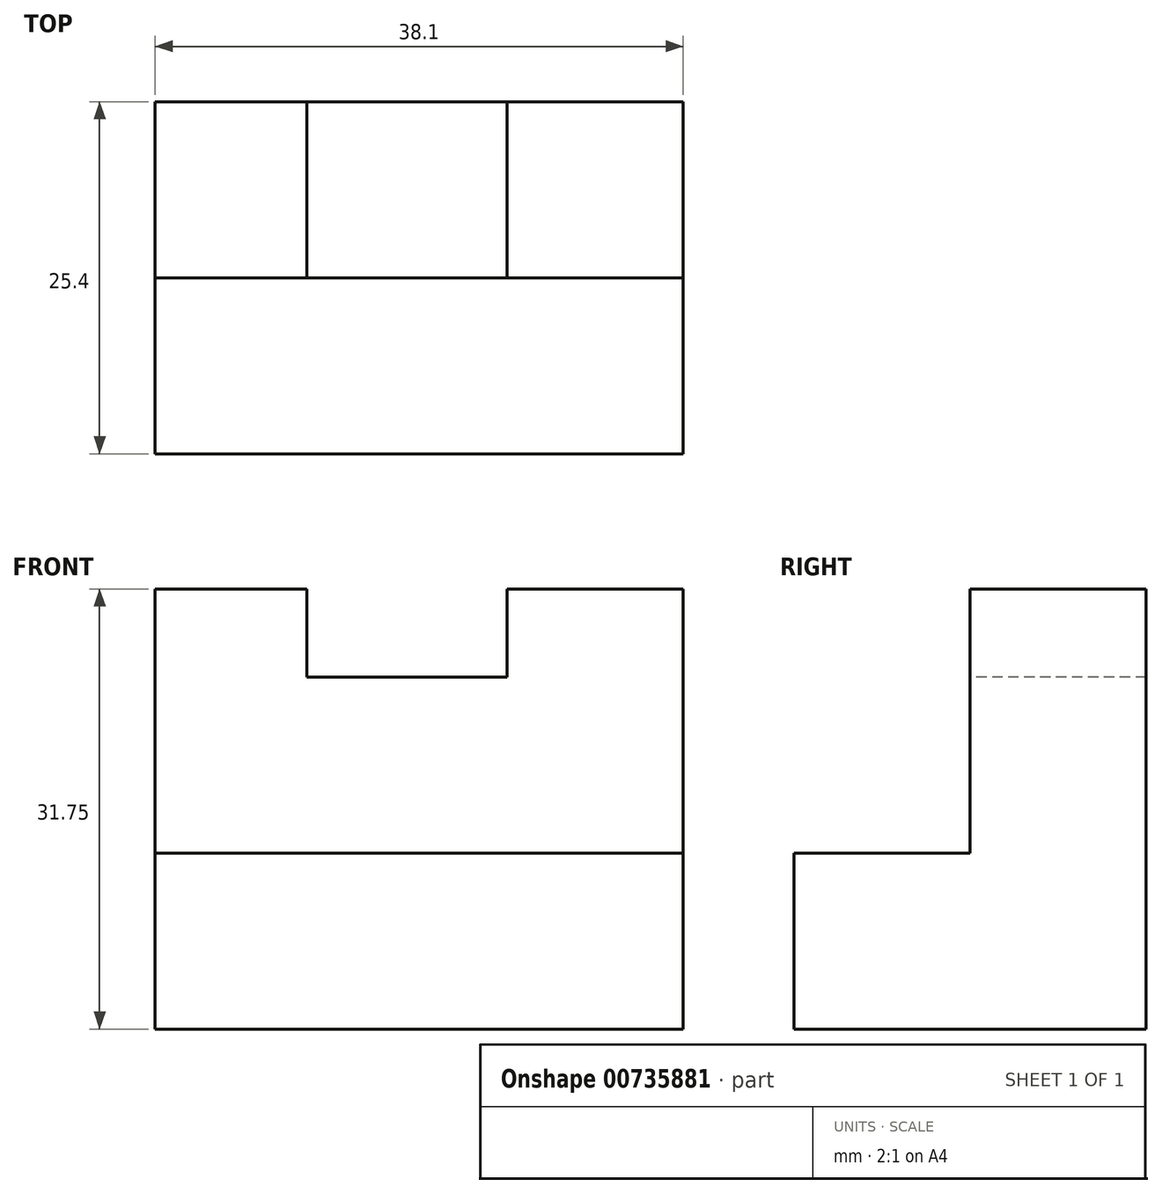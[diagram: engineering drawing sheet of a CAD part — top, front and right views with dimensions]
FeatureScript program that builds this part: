
annotation { "Feature Type Name" : "Feature", "Feature Type Description" : "" }
export const myFeature = defineFeature(function(context is Context, id is Id, definition is map)
    precondition{}
    {
        {
            var Q0;
            Q0=qCreatedBy(makeId("Right.planeOp"),FACE);
            var sketch = newSketch(context, id + "F0", { "sketchPlane" : qUnion([Q0])});
            skLineSegment(sketch, "E0", {"start": v(0, 0) * mm, "end": v(25.4, 0) * mm});
            skLineSegment(sketch, "E1", {"start": v(25.4, 0) * mm, "end": v(25.4, 31.75) * mm});
            skLineSegment(sketch, "E2", {"start": v(25.4, 31.75) * mm, "end": v(12.7, 31.75) * mm});
            skLineSegment(sketch, "E3", {"start": v(12.7, 31.75) * mm, "end": v(12.7, 12.7) * mm});
            skLineSegment(sketch, "E4", {"start": v(12.7, 12.7) * mm, "end": v(0, 12.7) * mm});
            skLineSegment(sketch, "E5", {"start": v(0, 12.7) * mm, "end": v(0, 0) * mm});
            skSolve(sketch);
        }
        {
            var Q0;
            Q0=makeQuery(id+"F0.imprint","IMPRINT",FACE,{"disambiguationData":[TD([[makeQuery(id+"F0.imprint","IMPRINT",EDGE,{"derivedFrom":sQuery(id+"F0.wireOp",EDGE,"E0")}),1.0]])]});
            extrude(context, id + "F1", {"entities" : qUnion([Q0]), "depth" : 38.1 * mm, "offsetDistance" : 25.4 * mm});
        }
        {
            var Q0;
            Q0=makeQuery(id+"F1.opExtrude","SWEPT_FACE",FACE,{"disambiguationData":[OSD([sQuery(id+"F0.wireOp",EDGE,"E3")])]});
            var sketch = newSketch(context, id + "F2", { "sketchPlane" : qUnion([Q0])});
            skLineSegment(sketch, "E6", {"start": v(19.05, 31.75) * mm, "end": v(19.05, 25.4) * mm});
            skLineSegment(sketch, "E7", {"start": v(19.05, 25.4) * mm, "end": v(25.4, 25.4) * mm});
            skLineSegment(sketch, "E8", {"start": v(25.4, 25.4) * mm, "end": v(25.4, 31.75) * mm});
            skSolve(sketch);
        }
        {
            var Q0;
            Q0 = qSketchRegion(id + "F2", true);
            var Q1;
            {var subQ0=sQuery(id+"F2.wireOp",EDGE,"E6");Q1=makeQuery(id+"F2.imprint","IMPRINT",FACE,{"disambiguationData":[TD([[makeQuery(id+"F2.imprint","IMPRINT",EDGE,{"derivedFrom":subQ0}),1.0]])]});}
            extrude(context, id + "F3", {"entities" : qUnion([Q0, Q1]), "operationType" : NewBodyOperationType.REMOVE, "oppositeDirection" : true, "depth" : 38.1 * mm, "offsetDistance" : 25.4 * mm});
        }
        {
            var Q0;
            Q0=makeQuery(id+"F1.opExtrude","SWEPT_FACE",FACE,{"disambiguationData":[OSD([sQuery(id+"F0.wireOp",EDGE,"E3")])]});
            var sketch = newSketch(context, id + "F4", { "sketchPlane" : qUnion([Q0])});
            skLineSegment(sketch, "E9", {"start": v(19.05, 25.4) * mm, "end": v(10.96, 25.4) * mm});
            skLineSegment(sketch, "E10", {"start": v(10.96, 25.4) * mm, "end": v(10.96, 31.75) * mm});
            skSolve(sketch);
        }
        {
            var Q0;
            Q0 = qSketchRegion(id + "F4", true);
            var Q1;
            Q1=makeQuery(id+"F4.imprint","IMPRINT",FACE,{"disambiguationData":[TD([[makeQuery(id+"F4.imprint","IMPRINT",EDGE,{"derivedFrom":sQuery(id+"F4.wireOp",EDGE,"E9")}),-1.0]])]});
            extrude(context, id + "F5", {"entities" : qUnion([Q0, Q1]), "operationType" : NewBodyOperationType.REMOVE, "oppositeDirection" : true, "depth" : 38.1 * mm, "offsetDistance" : 25.4 * mm});
        }
    });
